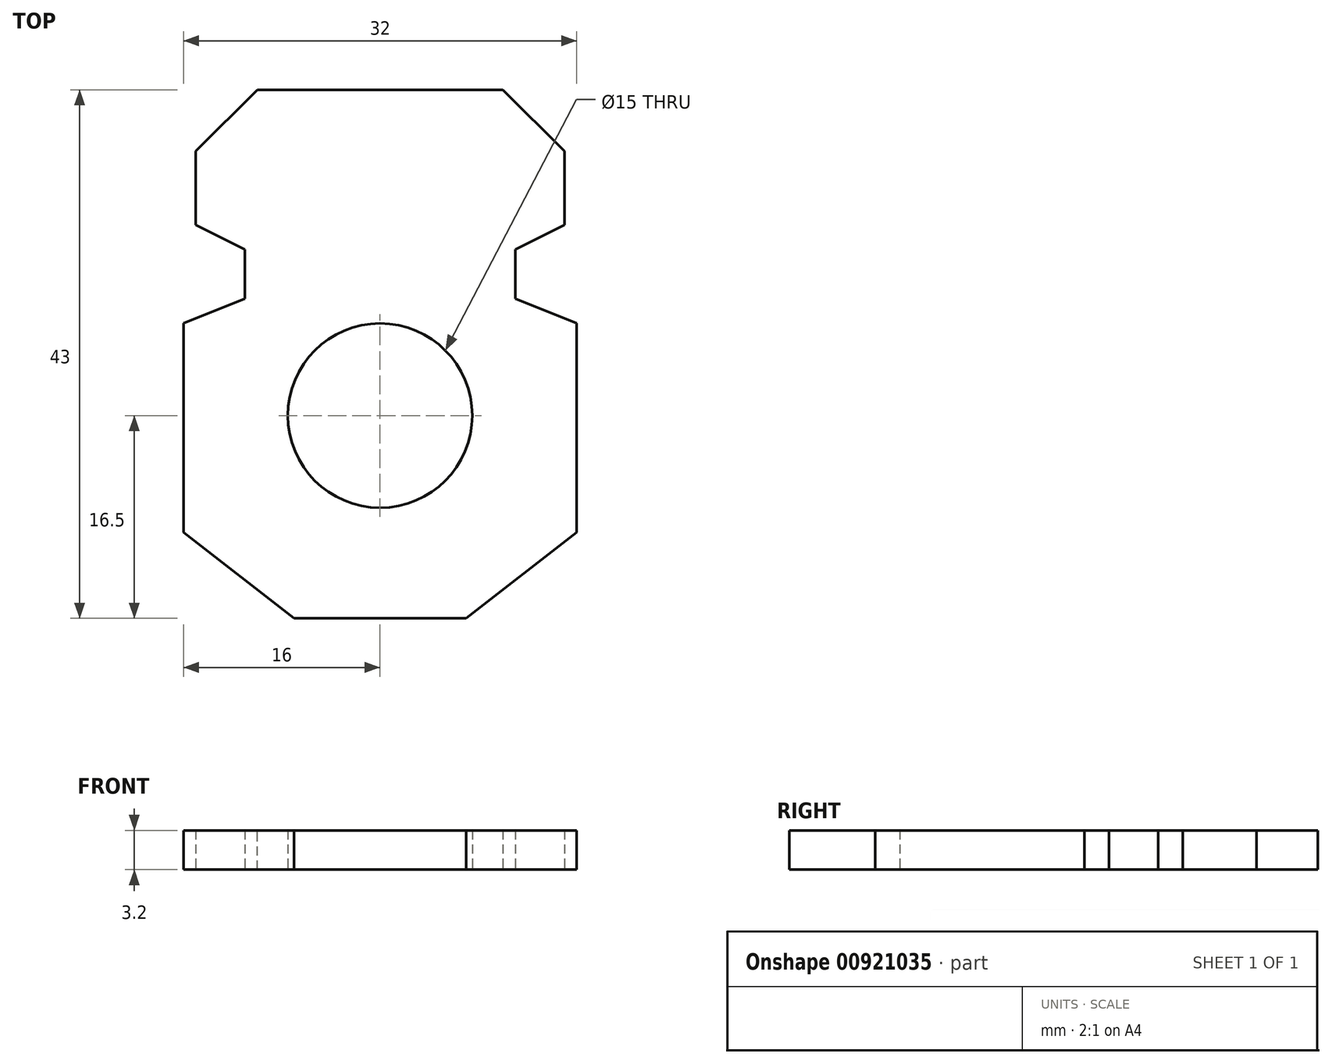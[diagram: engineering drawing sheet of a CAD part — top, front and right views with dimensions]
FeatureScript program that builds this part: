
annotation { "Feature Type Name" : "Feature", "Feature Type Description" : "" }
export const myFeature = defineFeature(function(context is Context, id is Id, definition is map)
    precondition{}
    {
        {
            var Q0;
            Q0=qCreatedBy(makeId("Top.planeOp"),FACE);
            var sketch = newSketch(context, id + "F0", { "sketchPlane" : qUnion([Q0])});
            skLineSegment(sketch, "E0", {"start": v(-16, -24) * mm, "end": v(-16, 0) * mm});
            skLineSegment(sketch, "E1", {"start": v(-15, 8) * mm, "end": v(-15, 19) * mm});
            skLineSegment(sketch, "E2", {"start": v(-15, 19) * mm, "end": v(15, 19) * mm});
            skLineSegment(sketch, "E3", {"start": v(15, 19) * mm, "end": v(15, 8) * mm});
            skLineSegment(sketch, "E4", {"start": v(16, 0) * mm, "end": v(16, -24) * mm});
            skLineSegment(sketch, "E5", {"start": v(16, -24) * mm, "end": v(-16, -24) * mm});
            skPoint(sketch, "E6.end.orphan", {"position": v(-11, 2) * mm});
            skPoint(sketch, "E7.end.orphan", {"position": v(11, 2) * mm});
            skLineSegment(sketch, "E8", {"start": v(-16, 0) * mm, "end": v(-11, 2) * mm});
            skLineSegment(sketch, "E9", {"start": v(-11, 2) * mm, "end": v(-11, 6) * mm});
            skLineSegment(sketch, "E10", {"start": v(-11, 6) * mm, "end": v(-15, 8) * mm});
            skLineSegment(sketch, "E11", {"start": v(16, 0) * mm, "end": v(11, 2) * mm});
            skLineSegment(sketch, "E12", {"start": v(11, 2) * mm, "end": v(11, 6) * mm});
            skLineSegment(sketch, "E13", {"start": v(11, 6) * mm, "end": v(15, 8) * mm});
            skCircle(sketch, "E14", {"center": v(0, -7.5) * mm, "radius": 7.5 * mm});
            skSolve(sketch);
        }
        {
            var Q0;
            Q0=makeQuery(id+"F0.imprint","IMPRINT",FACE,{"disambiguationData":[TD([[makeQuery(id+"F0.imprint","IMPRINT",EDGE,{"derivedFrom":sQuery(id+"F0.wireOp",EDGE,"E0")}),-1.0]])]});
            extrude(context, id + "F1", {"entities" : qUnion([Q0]), "depth" : 3.2 * mm, "offsetDistance" : 25 * mm});
        }
        {
            var Q0;
            Q0=makeQuery(id+"F1.opExtrude","SWEPT_EDGE",EDGE,{"disambiguationData":[OSD([sQuery(id+"F0.wireOp",EDGE,"E0"),sQuery(id+"F0.wireOp",EDGE,"E5")])]});
            var Q1;
            Q1=makeQuery(id+"F1.opExtrude","SWEPT_EDGE",EDGE,{"disambiguationData":[OSD([sQuery(id+"F0.wireOp",EDGE,"E4"),sQuery(id+"F0.wireOp",EDGE,"E5")])]});
            chamfer(context, id + "F2", {"entities" : qUnion([Q0, Q1]), "chamferType" : ChamferType.TWO_OFFSETS, "width1" : 9 * mm, "oppositeDirection" : false, "width2" : 7 * mm, "tangentPropagation" : true});
        }
        {
            var Q0;
            Q0=makeQuery(id+"F1.opExtrude","SWEPT_EDGE",EDGE,{"disambiguationData":[OSD([sQuery(id+"F0.wireOp",EDGE,"E1"),sQuery(id+"F0.wireOp",EDGE,"E2")])]});
            var Q1;
            Q1=makeQuery(id+"F1.opExtrude","SWEPT_EDGE",EDGE,{"disambiguationData":[OSD([sQuery(id+"F0.wireOp",EDGE,"E2"),sQuery(id+"F0.wireOp",EDGE,"E3")])]});
            chamfer(context, id + "F3", {"entities" : qUnion([Q0, Q1]), "width" : 5 * mm, "tangentPropagation" : true});
        }
    });
